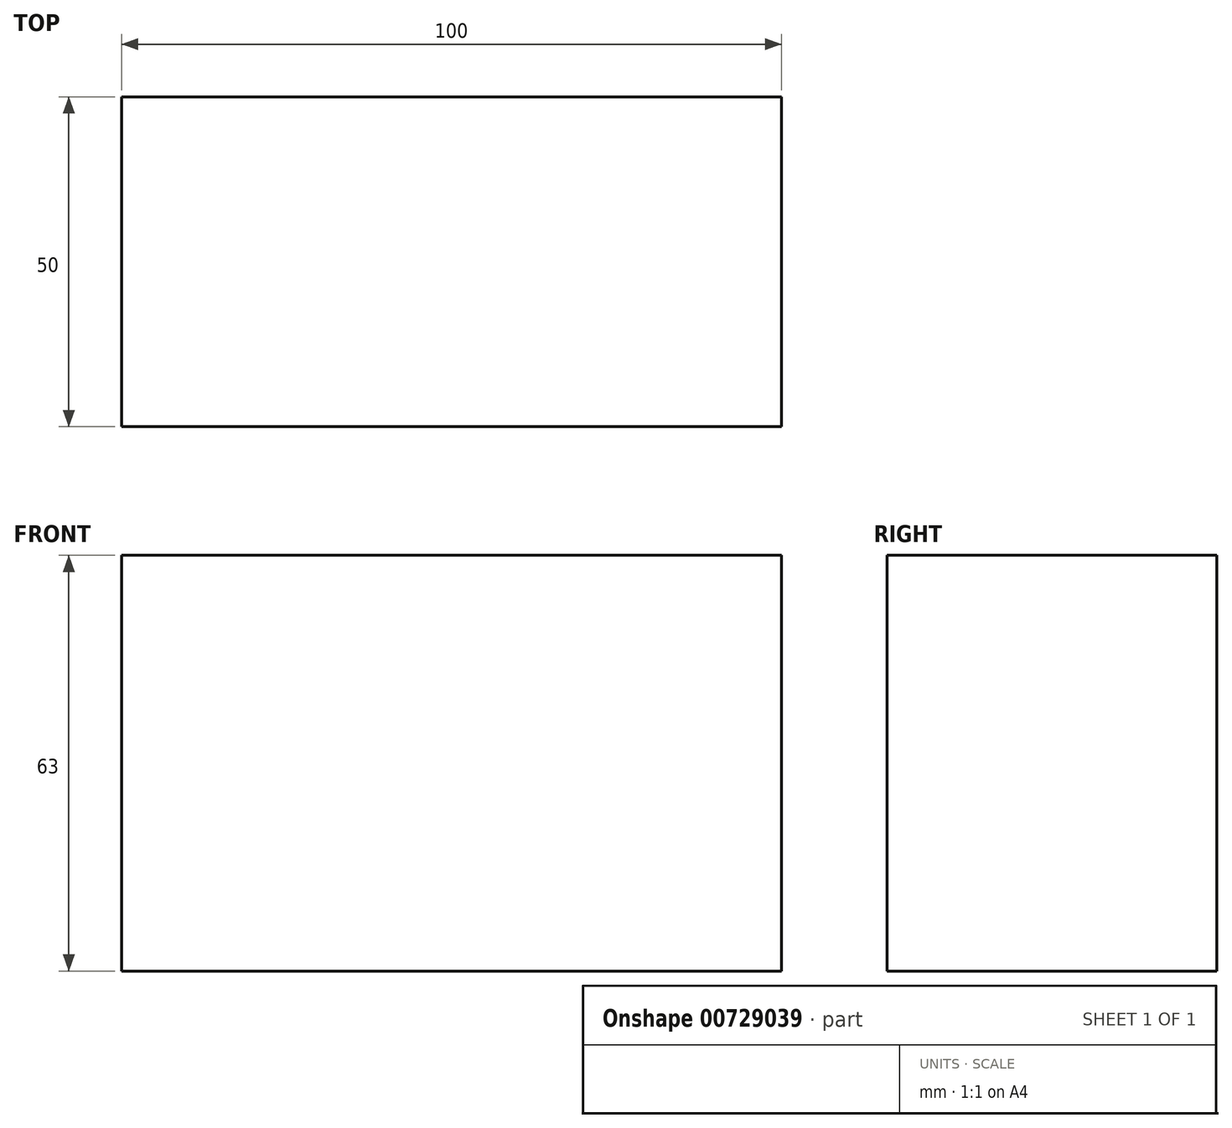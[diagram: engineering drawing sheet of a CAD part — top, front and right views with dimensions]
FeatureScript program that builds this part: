
annotation { "Feature Type Name" : "Feature", "Feature Type Description" : "" }
export const myFeature = defineFeature(function(context is Context, id is Id, definition is map)
    precondition{}
    {
        {
            var Q0;
            Q0=qCreatedBy(makeId("Front.planeOp"),FACE);
            var sketch = newSketch(context, id + "F0", { "sketchPlane" : qUnion([Q0])});
            skLineSegment(sketch, "E0", {"start": v(0, 0) * mm, "end": v(0, 63) * mm});
            skLineSegment(sketch, "E1", {"start": v(0, 63) * mm, "end": v(100, 63) * mm});
            skLineSegment(sketch, "E2", {"start": v(100, 63) * mm, "end": v(100, 0) * mm});
            skLineSegment(sketch, "E3", {"start": v(100, 0) * mm, "end": v(0, 0) * mm});
            skSolve(sketch);
        }
        {
            var Q0;
            Q0 = qSketchRegion(id + "F0", true);
            extrude(context, id + "F1", {"entities" : qUnion([Q0]), "depth" : 50 * mm, "offsetDistance" : 25 * mm});
        }
    });
